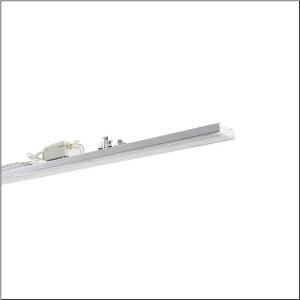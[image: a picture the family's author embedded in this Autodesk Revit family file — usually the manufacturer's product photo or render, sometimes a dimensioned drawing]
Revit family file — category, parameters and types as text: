
# Revit family: licross_11_recessed_mo_51tl18de445g
name_source: partatom
category: Lighting Fixtures
units: mm (PartAtom-declared; Revit-internal decimal feet)

## family parameters
Cut with Voids When Loaded = No
Host = Face
Light Source = No
Part Type = Normal
Room Calculation Point = No
Round Connector Dimension = Use Diameter
Shared = No

## types (1)
- --- (1 x LED, 4970 lm, 29.6 W, 4000K)
    Apparent Load = 30 VA
    CIE Flux Codes = 83 96 99 100 100
    Color Rendering = 80
    Color Temperature = 4000K
    Default Elevation = 1800 mm
    Description = Licross 11 Recessed MO, luminaire insert, of sheet steel, coil coated, white, length: 750mm, width: 66mm, height: 67mm, LED rated luminous flux: 4.970lm, light colour: 840, SDCM (Standard Deviation of Colour Matching)MacAdam ≤ 2 SDCM (initial), control gear: DALI 2, with plug, 5-pole, with phase selection, mains connection: 220..240V, AC, 50/60Hz, rated input power: 30W, internal wiring halogen-free, primary light control with lens, of plastic, primary optical cover: cover, of PMMA, light emission: direct distribution, primary light characteristic: symmetric, protection rating (complete): IP40, insulation class (complete): insulation class I (protective earthing), certification: CE, ENEC, VDE, UKCA, protection symbol: D if used in an environment without relevant dust loads with corresponding accessories, impact resistance: IK06, permissible ambient temperature for indoor applications: -25..+35°C, corresponds to IFS (International Featured Standards) requirements for safety and quality in the food industry, reducing of maximum allowable ambient temperature of 5°C with ceiling mounting, LABS conformity tested according to VDMA 24364:2018-05, The light source and the operating device comply with the requirements of the Ecodesign Regulation (EU) 2019/2020 and are replaceable in accordance with this regulation, packaging unit: 1 piece
    Height = 58 mm
    Lamp = 1 x LED
    Lamp Light Flux = 4970 lm
    Lamp Power = 29.6 W
    Lamp count = 1
    Length = 750 mm
    Luminous efficacy = 168 lm/W
    Manufacturer = Siteco
    ModVariant = No
    Model = 51TL18DE445G
    Mounting Place = Ceiling
    Mounting Type = Pendant
    Number of Poles = 1
    OnlyDefault = Yes
    Power Factor = 1
    Product Name = Licross 11 Recessed MO
    Product group = luminaire insert | ceiling pendant
    ProductGroupID = 901
    Protection Class = Protection class I
    Protection Degree = IP 40
    RLX_Detail_Level = 1
    RLX_Emergency_Light_Flux = 0 lm
    RLX_Emergency_Type = 0
    RLX_Emergency_Type_DB = No
    RlxData = <blob elided: 29473 chars, md5=8d314c93>
    Socket = socket
    Standby Power = 0 W
    System Light Flux = 4970 lm
    System Power = 30 W
    Type Comments = factory setting: luminous flux: 100 % | dim-lin: 254 | 378 mA
    Type Image = l_1296930.jpg
    URL = http://relux.com
    VarID = @adj_102085
    Voltage = 0 V
    Weight = 0.00 kg
    Width = 66 mm

## geometry (parser evidence)
native form markers: Blend x4, Sweep x10
no freeform markers — native parametric forms only
